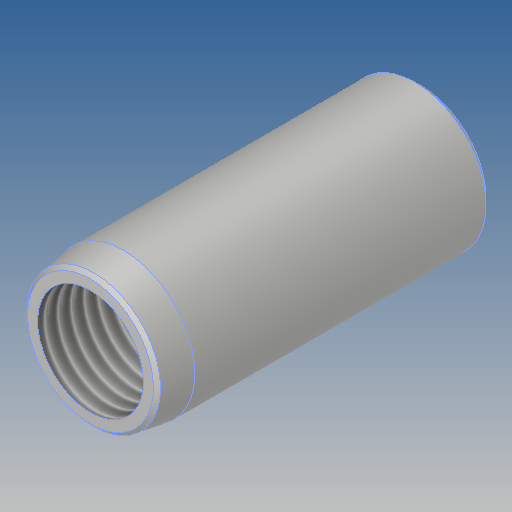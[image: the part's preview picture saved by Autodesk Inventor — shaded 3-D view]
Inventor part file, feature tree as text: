
AUTODESK INVENTOR PART (.ipt)
format: ipt  version: 2019 (Build 230136000, 136)  size: 175,616 bytes
history: native  units: mm
features: other x3, chamfer x1, sketch x1
ambient origin geometry x8: Origin, YZ Plane, XZ Plane, XY Plane, X Axis, Y Axis, Z Axis, Center Point
bodies: Solide1 (feature_tree)
feature tree (5):
  other  "Révolution1"
  other  "Filetage1"
  other  "Plan de construction2"
  chamfer  "Chanfrein4"  Distance=27.925268mm
  sketch  "Esquisse1"
